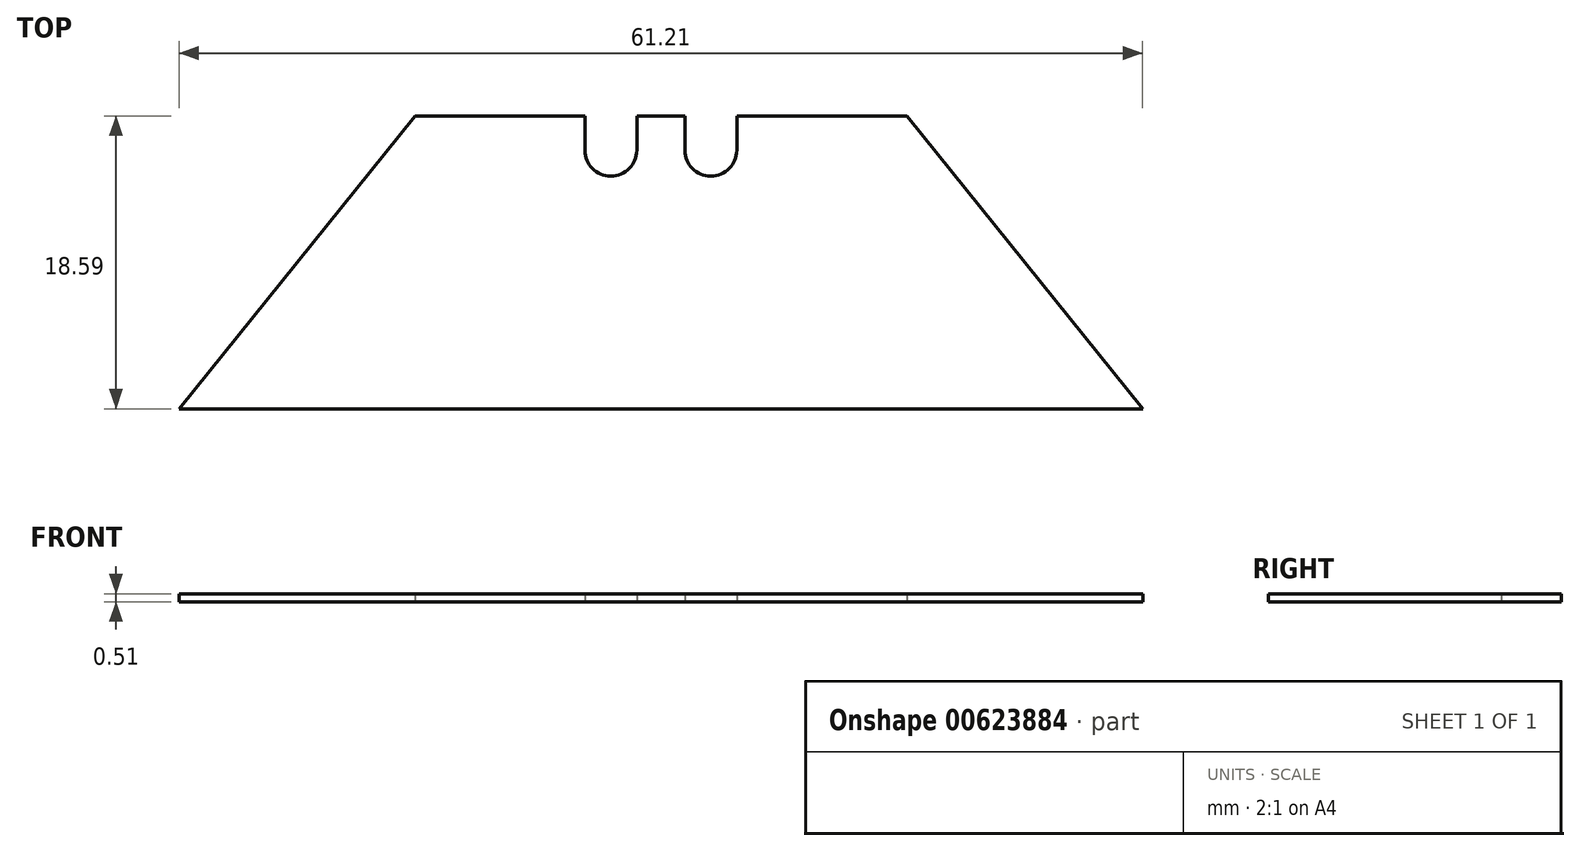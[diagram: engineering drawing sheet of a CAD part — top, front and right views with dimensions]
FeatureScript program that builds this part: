
annotation { "Feature Type Name" : "Feature", "Feature Type Description" : "" }
export const myFeature = defineFeature(function(context is Context, id is Id, definition is map)
    precondition{}
    {
        {
            var Q0;
            Q0=qCreatedBy(makeId("Top.planeOp"),FACE);
            var sketch = newSketch(context, id + "F0", { "sketchPlane" : qUnion([Q0])});
            skLineSegment(sketch, "E0", {"start": v(0, 0) * mm, "end": v(61.21, 0) * mm});
            skLineSegment(sketch, "E1", {"start": v(0, 0) * mm, "end": v(14.99, 18.59) * mm});
            skLineSegment(sketch, "E2", {"start": v(46.23, 18.59) * mm, "end": v(61.21, 0) * mm});
            skLineSegment(sketch, "E3", {"start": v(14.99, 18.59) * mm, "end": v(25.78, 18.59) * mm});
            skLineSegment(sketch, "E4", {"start": v(46.23, 18.59) * mm, "end": v(35.43, 18.59) * mm});
            skLineSegment(sketch, "E5", {"start": v(35.43, 18.59) * mm, "end": v(35.43, 16.42) * mm});
            skLineSegment(sketch, "E6", {"start": v(32.13, 16.42) * mm, "end": v(32.13, 18.59) * mm});
            skLineSegment(sketch, "E7", {"start": v(25.78, 18.59) * mm, "end": v(25.78, 16.42) * mm});
            skLineSegment(sketch, "E8", {"start": v(29.08, 16.42) * mm, "end": v(29.08, 18.59) * mm});
            skArc(sketch, "E9", {"start": v(25.78, 16.42) * mm, "mid": v(27.43, 14.77) * mm, "end": v(29.08, 16.42) * mm});
            skArc(sketch, "E10", {"start": v(32.13, 16.42) * mm, "mid": v(33.78, 14.77) * mm, "end": v(35.43, 16.42) * mm});
            skLineSegment(sketch, "E11.trimOffspring", {"start": v(35.43, 18.59) * mm, "end": v(46.23, 18.59) * mm});
            skLineSegment(sketch, "E12.trimOffspring", {"start": v(29.08, 18.59) * mm, "end": v(32.13, 18.59) * mm});
            skSolve(sketch);
        }
        {
            var Q0;
            Q0=makeQuery(id+"F0.imprint","IMPRINT",FACE,{"disambiguationData":[TD([[makeQuery(id+"F0.imprint","IMPRINT",EDGE,{"derivedFrom":sQuery(id+"F0.wireOp",EDGE,"E0")}),1.0]])]});
            extrude(context, id + "F1", {"entities" : qUnion([Q0]), "depth" : 0.5 * mm, "offsetDistance" : 25.4 * mm});
        }
    });
